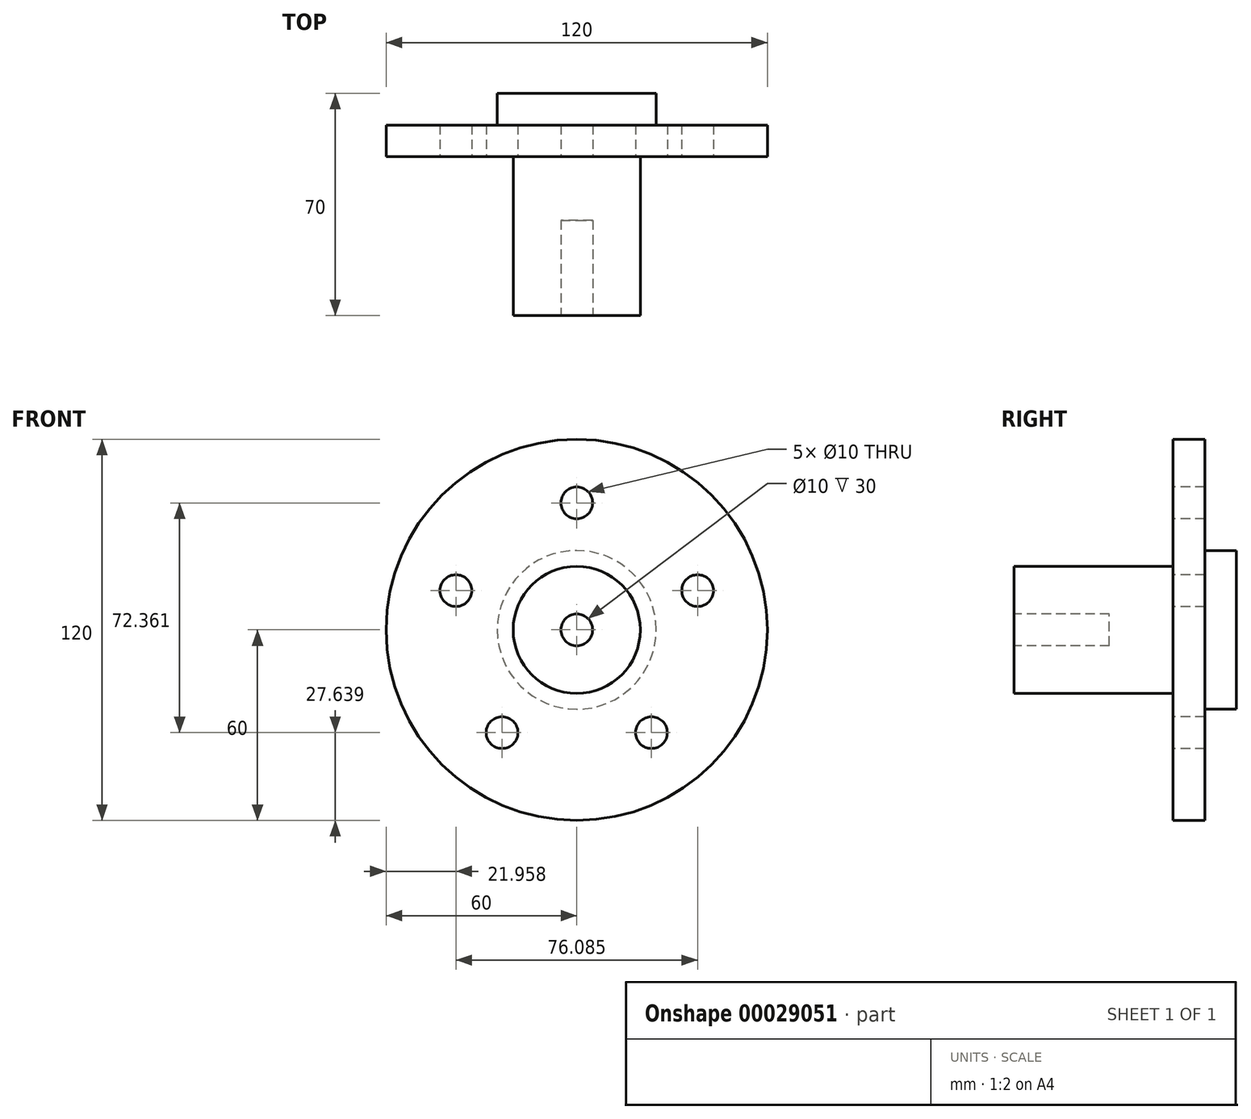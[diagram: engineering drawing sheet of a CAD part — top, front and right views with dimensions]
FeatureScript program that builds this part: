
annotation { "Feature Type Name" : "Feature", "Feature Type Description" : "" }
export const myFeature = defineFeature(function(context is Context, id is Id, definition is map)
    precondition{}
    {
        {
            var Q0;
            Q0=qCreatedBy(makeId("Front.planeOp"),FACE);
            var sketch = newSketch(context, id + "F0", { "sketchPlane" : qUnion([Q0])});
            skCircle(sketch, "E0", {"center": v(0, 0) * mm, "radius": 25 * mm});
            skSolve(sketch);
        }
        {
            var Q0;
            Q0 = qSketchRegion(id + "F0", true);
            extrude(context, id + "F1", {"entities" : qUnion([Q0]), "oppositeDirection" : true, "depth" : 10 * mm});
        }
        {
            var Q0;
            Q0=qCreatedBy(makeId("Front.planeOp"),FACE);
            var sketch = newSketch(context, id + "F2", { "sketchPlane" : qUnion([Q0])});
            skCircle(sketch, "E1", {"center": v(0, 0) * mm, "radius": 60 * mm});
            skSolve(sketch);
        }
        {
            var Q0;
            Q0=makeQuery(id+"F2.imprint","IMPRINT",FACE,{"disambiguationData":[TD([[makeQuery(id+"F2.imprint","IMPRINT",EDGE,{"derivedFrom":sQuery(id+"F2.wireOp",EDGE,"E1")}),1.0]])]});
            extrude(context, id + "F3", {"entities" : qUnion([Q0]), "operationType" : NewBodyOperationType.ADD, "depth" : 10 * mm});
        }
        {
            var Q0;
            Q0=makeQuery(id+"F3.opExtrude","CAP_FACE",FACE,{"disambiguationData":[OSD([sQuery(id+"F2.wireOp",EDGE,"E1")])],"isStart":false});
            var sketch = newSketch(context, id + "F4", { "sketchPlane" : qUnion([Q0])});
            skCircle(sketch, "E2", {"center": v(0, 40) * mm, "radius": 5 * mm});
            skCircle(sketch, "E3.1.0", {"center": v(-38.04, 12.36) * mm, "radius": 5 * mm});
            skCircle(sketch, "E3.2.0", {"center": v(-23.51, -32.36) * mm, "radius": 5 * mm});
            skCircle(sketch, "E3.3.0", {"center": v(23.51, -32.36) * mm, "radius": 5 * mm});
            skCircle(sketch, "E3.4.0", {"center": v(38.04, 12.36) * mm, "radius": 5 * mm});
            skPoint(sketch, "E3.center", {"position": v(0, 0) * mm});
            skSolve(sketch);
        }
        {
            var Q0;
            Q0 = qSketchRegion(id + "F4", true);
            extrude(context, id + "F5", {"entities" : qUnion([Q0]), "operationType" : NewBodyOperationType.REMOVE, "endBound" : BoundingType.THROUGH_ALL, "oppositeDirection" : true, "depth" : 25 * mm});
        }
        {
            var Q0;
            Q0=makeQuery(id+"F3.opExtrude","CAP_FACE",FACE,{"disambiguationData":[OSD([sQuery(id+"F2.wireOp",EDGE,"E1")])],"isStart":false});
            var sketch = newSketch(context, id + "F6", { "sketchPlane" : qUnion([Q0])});
            skCircle(sketch, "E4", {"center": v(0, 0) * mm, "radius": 20 * mm});
            skSolve(sketch);
        }
        {
            var Q0;
            Q0 = qSketchRegion(id + "F6", true);
            extrude(context, id + "F7", {"entities" : qUnion([Q0]), "operationType" : NewBodyOperationType.ADD, "depth" : 50 * mm});
        }
        {
            var Q0;
            Q0=makeQuery(id+"F7.opExtrude","CAP_FACE",FACE,{"disambiguationData":[OSD([sQuery(id+"F6.wireOp",EDGE,"E4")])],"isStart":false});
            var sketch = newSketch(context, id + "F8", { "sketchPlane" : qUnion([Q0])});
            skCircle(sketch, "E5", {"center": v(0, 0) * mm, "radius": 5 * mm});
            skSolve(sketch);
        }
        {
            var Q0;
            Q0=makeQuery(id+"F8.imprint","IMPRINT",FACE,{"disambiguationData":[TD([[makeQuery(id+"F8.imprint","IMPRINT",EDGE,{"derivedFrom":sQuery(id+"F8.wireOp",EDGE,"E5")}),1.0]])]});
            var Q1;
            Q1=sQuery(id+"F8.wireOp",EDGE,"E5");
            extrude(context, id + "F9", {"entities" : qUnion([Q0]), "operationType" : NewBodyOperationType.REMOVE, "surfaceEntities" : qUnion([Q1]), "oppositeDirection" : true, "depth" : 30 * mm});
        }
    });
